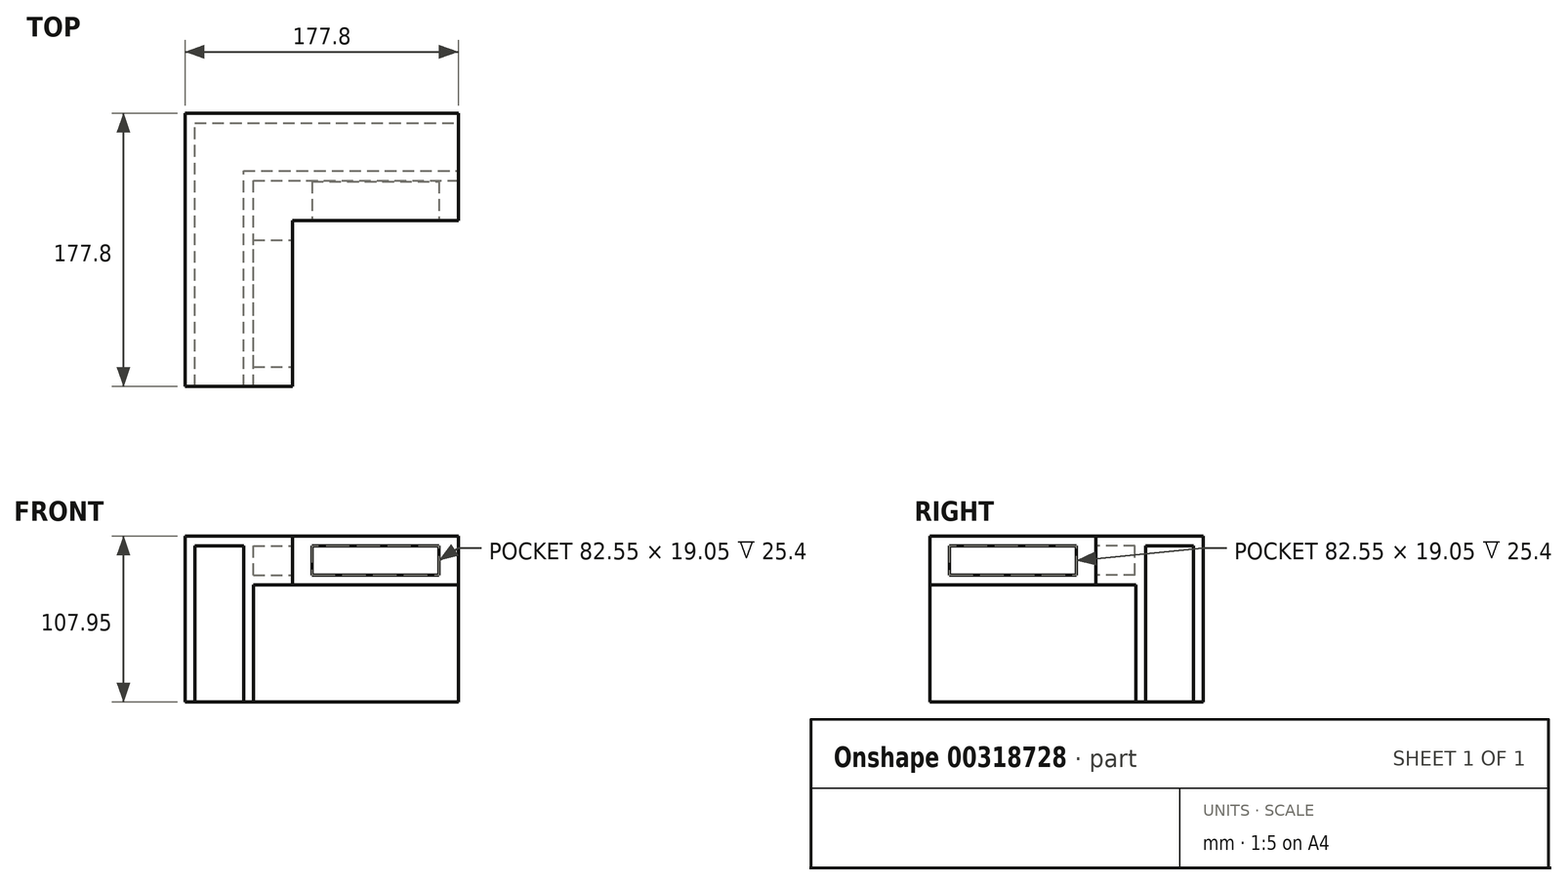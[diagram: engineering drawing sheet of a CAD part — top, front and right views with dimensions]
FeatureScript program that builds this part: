
annotation { "Feature Type Name" : "Feature", "Feature Type Description" : "" }
export const myFeature = defineFeature(function(context is Context, id is Id, definition is map)
    precondition{}
    {
        {
            var Q0;
            Q0=qCreatedBy(makeId("Top.planeOp"),FACE);
            var sketch = newSketch(context, id + "F0", { "sketchPlane" : qUnion([Q0])});
            skLineSegment(sketch, "E0", {"start": v(0, 0) * mm, "end": v(0, -177.8) * mm});
            skLineSegment(sketch, "E1", {"start": v(0, -177.8) * mm, "end": v(44.45, -177.8) * mm});
            skLineSegment(sketch, "E2", {"start": v(44.45, -177.8) * mm, "end": v(44.45, -44.45) * mm});
            skLineSegment(sketch, "E3", {"start": v(44.45, -44.45) * mm, "end": v(177.8, -44.45) * mm});
            skLineSegment(sketch, "E4", {"start": v(177.8, -44.45) * mm, "end": v(177.8, 0) * mm});
            skLineSegment(sketch, "E5", {"start": v(177.8, 0) * mm, "end": v(0, 0) * mm});
            skLineSegment(sketch, "E6", {"start": v(0, -177.8) * mm, "end": v(6.35, -177.8) * mm});
            skLineSegment(sketch, "E7", {"start": v(6.35, -177.8) * mm, "end": v(6.35, -6.35) * mm});
            skLineSegment(sketch, "E8", {"start": v(6.35, -6.35) * mm, "end": v(177.8, -6.35) * mm});
            skLineSegment(sketch, "E9", {"start": v(177.8, -6.35) * mm, "end": v(177.8, 0) * mm});
            skLineSegment(sketch, "E10", {"start": v(44.45, -177.8) * mm, "end": v(38.1, -177.8) * mm});
            skLineSegment(sketch, "E11", {"start": v(38.1, -177.8) * mm, "end": v(38.1, -37.58) * mm});
            skLineSegment(sketch, "E12", {"start": v(38.1, -37.58) * mm, "end": v(177.8, -37.58) * mm});
            skLineSegment(sketch, "E13", {"start": v(177.8, -37.58) * mm, "end": v(177.8, -44.45) * mm});
            skLineSegment(sketch, "E14", {"start": v(44.45, -44.45) * mm, "end": v(44.45, -177.8) * mm});
            skSolve(sketch);
        }
        {
            var Q0;
            {var subQ4=sQuery(id+"F0.wireOp",EDGE,"E0");Q0=makeQuery(id+"F0.imprint","IMPRINT",FACE,{"disambiguationData":[TD([[makeQuery(id+"F0.imprint","IMPRINT",EDGE,{"derivedFrom":subQ4}),1.0]])]});}
            var Q1;
            {var subQ0=sQuery(id+"F0.wireOp",EDGE,"E7");Q1=makeQuery(id+"F0.imprint","IMPRINT",FACE,{"disambiguationData":[TD([[makeQuery(id+"F0.imprint","IMPRINT",EDGE,{"derivedFrom":subQ0}),-1.0]])]});}
            var Q2;
            {var subQ3=sQuery(id+"F0.wireOp",EDGE,"E2");Q2=makeQuery(id+"F0.imprint","IMPRINT",FACE,{"disambiguationData":[TD([[makeQuery(id+"F0.imprint","IMPRINT",EDGE,{"derivedFrom":subQ3}),1.0]])]});}
            extrude(context, id + "F1", {"entities" : qUnion([Q0, Q1, Q2]), "depth" : 6.35 * mm, "offsetDistance" : 25.4 * mm});
        }
        {
            var Q0;
            {var subQ4=sQuery(id+"F0.wireOp",EDGE,"E0");Q0=makeQuery(id+"F0.imprint","IMPRINT",FACE,{"disambiguationData":[TD([[makeQuery(id+"F0.imprint","IMPRINT",EDGE,{"derivedFrom":subQ4}),1.0]])]});}
            var Q1;
            {var subQ3=sQuery(id+"F0.wireOp",EDGE,"E2");Q1=makeQuery(id+"F0.imprint","IMPRINT",FACE,{"disambiguationData":[TD([[makeQuery(id+"F0.imprint","IMPRINT",EDGE,{"derivedFrom":subQ3}),1.0]])]});}
            extrude(context, id + "F2", {"entities" : qUnion([Q0, Q1]), "operationType" : NewBodyOperationType.ADD, "oppositeDirection" : true, "depth" : 101.6 * mm, "offsetDistance" : 25.4 * mm});
        }
        {
            var Q0;
            {var subQ0=sQuery(id+"F0.wireOp",EDGE,"E3");Q0=makeQuery(id+"F2.boolean.opBoolean","MERGE",FACE,{"derivedFrom":[makeQuery(id+"F1.opExtrude","SWEPT_FACE",FACE,{"disambiguationData":[OSD([subQ0])]}),makeQuery(id+"F2.opExtrude","SWEPT_FACE",FACE,{"disambiguationData":[OSD([subQ0])]})]});}
            extrude(context, id + "F3", {"entities" : qUnion([Q0]), "operationType" : NewBodyOperationType.ADD, "depth" : 25.4 * mm, "offsetDistance" : 25.4 * mm});
        }
        {
            var Q0;
            {var subQ0=sQuery(id+"F0.wireOp",EDGE,"E2");Q0=makeQuery(id+"F2.boolean.opBoolean","MERGE",FACE,{"derivedFrom":[makeQuery(id+"F1.opExtrude","SWEPT_FACE",FACE,{"disambiguationData":[OSD([subQ0])]}),makeQuery(id+"F2.opExtrude","SWEPT_FACE",FACE,{"disambiguationData":[OSD([subQ0])]})]});}
            extrude(context, id + "F4", {"entities" : qUnion([Q0]), "operationType" : NewBodyOperationType.ADD, "depth" : 25.4 * mm, "offsetDistance" : 25.4 * mm});
        }
        {
            var Q0;
            {var subQ0=sQuery(id+"F0.wireOp",EDGE,"E2");var subQ1=sQuery(id+"F0.wireOp",EDGE,"E3");Q0=makeQuery(id+"F4.boolean.opBoolean","MERGE",FACE,{"derivedFrom":[makeQuery(id+"F3.boolean.opBoolean","MERGE",FACE,{"derivedFrom":[makeQuery(id+"F2.opExtrude","CAP_FACE",FACE,{"disambiguationData":[OSD([sQuery(id+"F0.wireOp",EDGE,"E1"),subQ0,subQ1,sQuery(id+"F0.wireOp",EDGE,"E4"),sQuery(id+"F0.wireOp",EDGE,"E11"),sQuery(id+"F0.wireOp",EDGE,"E12")])],"isStart":false}),makeQuery(id+"F3.opExtrude","SWEPT_FACE",FACE,{"disambiguationData":[OSD([subQ1]),TDD([makeQuery(id+"F2.opExtrude","CAP_EDGE",EDGE,{"disambiguationData":[OSD([subQ1])],"isStart":false})])]})]}),makeQuery(id+"F4.opExtrude","SWEPT_FACE",FACE,{"disambiguationData":[OSD([subQ0]),TDD([makeQuery(id+"F2.opExtrude","CAP_EDGE",EDGE,{"disambiguationData":[OSD([subQ0])],"isStart":false})])]})]});}
            var sketch = newSketch(context, id + "F5", { "sketchPlane" : qUnion([Q0])});
            skLineSegment(sketch, "E15", {"start": v(38.1, 177.8) * mm, "end": v(44.45, 177.8) * mm});
            skLineSegment(sketch, "E16", {"start": v(44.45, 177.8) * mm, "end": v(44.45, 43.93) * mm});
            skLineSegment(sketch, "E17", {"start": v(44.45, 43.93) * mm, "end": v(177.8, 43.93) * mm});
            skLineSegment(sketch, "E18", {"start": v(177.8, 43.93) * mm, "end": v(177.8, 37.58) * mm});
            skLineSegment(sketch, "E19", {"start": v(177.8, 37.58) * mm, "end": v(38.1, 37.58) * mm});
            skLineSegment(sketch, "E20", {"start": v(38.1, 37.58) * mm, "end": v(38.1, 177.8) * mm});
            skSolve(sketch);
        }
        {
            var Q0;
            {var subQ7=sQuery(id+"F5.wireOp",EDGE,"E16");Q0=makeQuery(id+"F5.imprint","IMPRINT",FACE,{"disambiguationData":[TD([[makeQuery(id+"F5.imprint","IMPRINT",EDGE,{"derivedFrom":subQ7}),1.0]])]});}
            extrude(context, id + "F6", {"entities" : qUnion([Q0]), "operationType" : NewBodyOperationType.REMOVE, "oppositeDirection" : true, "depth" : 76.2 * mm, "offsetDistance" : 25.4 * mm});
        }
        {
            var Q0;
            Q0=makeQuery(id+"F4.opExtrude","CAP_FACE",FACE,{"disambiguationData":[OSD([sQuery(id+"F0.wireOp",EDGE,"E2")])],"isStart":false});
            var sketch = newSketch(context, id + "F7", { "sketchPlane" : qUnion([Q0])});
            skLineSegment(sketch, "E21.bottom", {"start": v(-165.1, -19.05) * mm, "end": v(-82.55, -19.05) * mm});
            skLineSegment(sketch, "E21.top", {"start": v(-165.1, 0) * mm, "end": v(-82.55, 0) * mm});
            skLineSegment(sketch, "E21.left", {"start": v(-165.1, -19.05) * mm, "end": v(-165.1, 0) * mm});
            skLineSegment(sketch, "E21.right", {"start": v(-82.55, -19.05) * mm, "end": v(-82.55, 0) * mm});
            skSolve(sketch);
        }
        {
            var Q0;
            Q0 = qSketchRegion(id + "F7", true);
            extrude(context, id + "F8", {"entities" : qUnion([Q0]), "operationType" : NewBodyOperationType.REMOVE, "oppositeDirection" : true, "depth" : 25.4 * mm, "offsetDistance" : 25.4 * mm});
        }
        {
            var Q0;
            Q0=makeQuery(id+"F3.opExtrude","CAP_FACE",FACE,{"disambiguationData":[OSD([sQuery(id+"F0.wireOp",EDGE,"E3")])],"isStart":false});
            var sketch = newSketch(context, id + "F9", { "sketchPlane" : qUnion([Q0])});
            skLineSegment(sketch, "E22.bottom", {"start": v(82.55, -19.05) * mm, "end": v(165.1, -19.05) * mm});
            skLineSegment(sketch, "E22.top", {"start": v(82.55, 0) * mm, "end": v(165.1, 0) * mm});
            skLineSegment(sketch, "E22.left", {"start": v(82.55, -19.05) * mm, "end": v(82.55, 0) * mm});
            skLineSegment(sketch, "E22.right", {"start": v(165.1, -19.05) * mm, "end": v(165.1, 0) * mm});
            skSolve(sketch);
        }
        {
            var Q0;
            Q0 = qSketchRegion(id + "F9", true);
            extrude(context, id + "F10", {"entities" : qUnion([Q0]), "operationType" : NewBodyOperationType.REMOVE, "oppositeDirection" : true, "depth" : 25.4 * mm, "offsetDistance" : 25.4 * mm});
        }
    });
